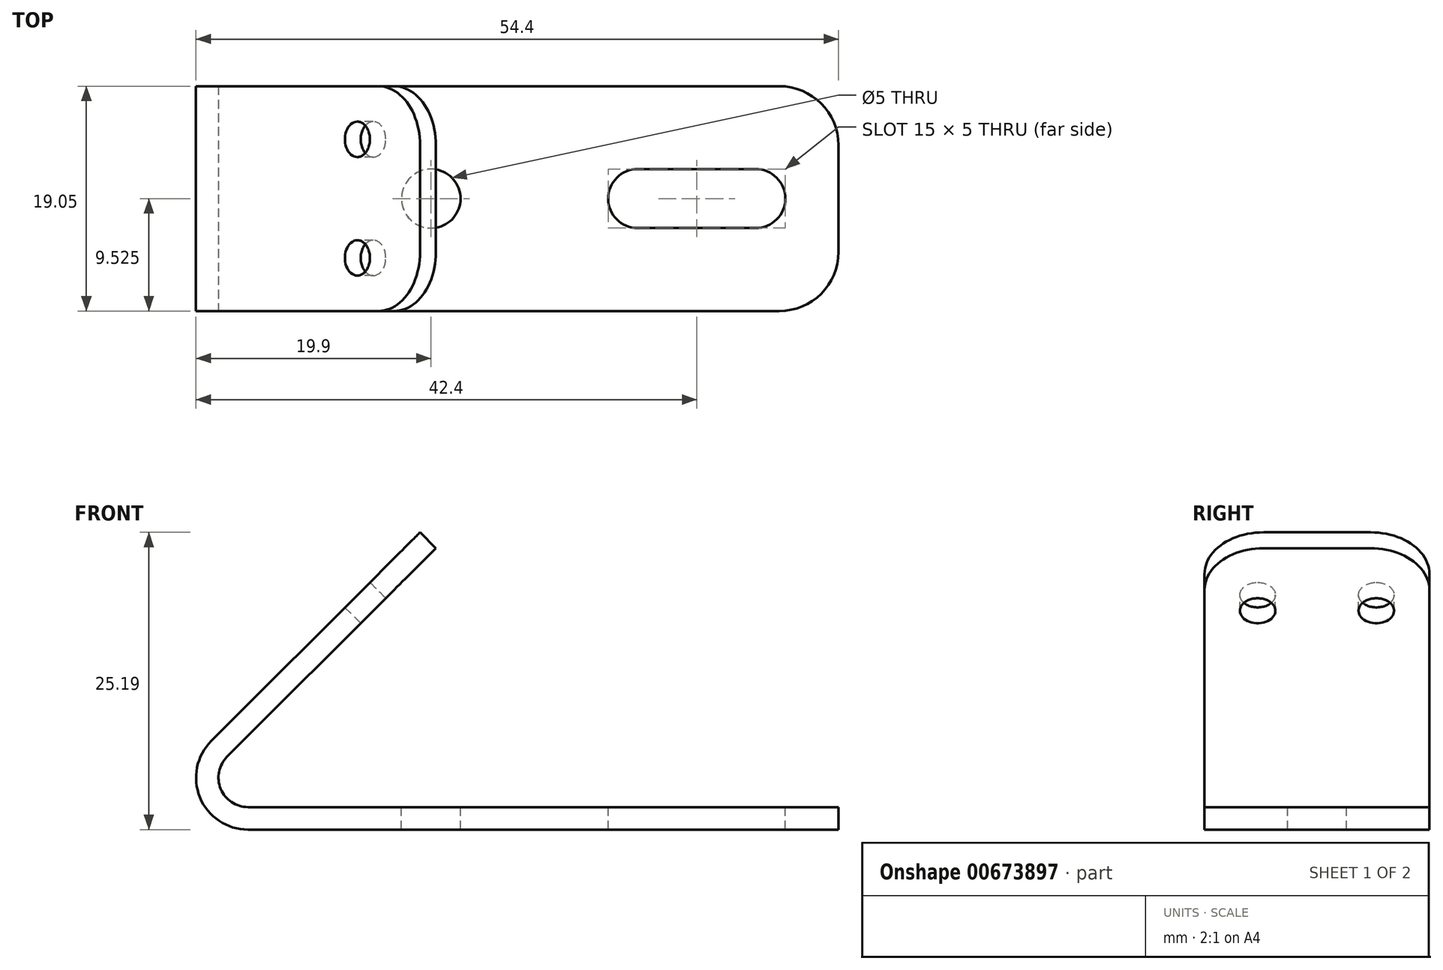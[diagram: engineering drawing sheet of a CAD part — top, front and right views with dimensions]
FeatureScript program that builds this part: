
annotation { "Feature Type Name" : "Feature", "Feature Type Description" : "" }
export const myFeature = defineFeature(function(context is Context, id is Id, definition is map)
    precondition{}
    {
        {
            var Q0;
            Q0=qCreatedBy(makeId("Front.planeOp"),FACE);
            var sketch = newSketch(context, id + "F0", { "sketchPlane" : qUnion([Q0])});
            skLineSegment(sketch, "E0", {"start": v(0, 0) * mm, "end": v(-50, 0) * mm});
            skLineSegment(sketch, "E1", {"start": v(-35.43, 25.19) * mm, "end": v(-53.11, 7.51) * mm});
            skArc(sketch, "E2", {"start": v(-53.11, 7.51) * mm, "mid": v(-54.07, 2.72) * mm, "end": v(-50, 0) * mm});
            skArc(sketch, "E3", {"start": v(-51.77, 6.17) * mm, "mid": v(-52.3, 3.44) * mm, "end": v(-50, 1.9) * mm});
            skLineSegment(sketch, "E4", {"start": v(-50, 1.9) * mm, "end": v(0, 1.9) * mm});
            skLineSegment(sketch, "E5", {"start": v(0, 1.9) * mm, "end": v(0, 0) * mm});
            skLineSegment(sketch, "E6", {"start": v(-35.43, 25.19) * mm, "end": v(-34.1, 23.85) * mm});
            skLineSegment(sketch, "E7", {"start": v(-34.1, 23.85) * mm, "end": v(-51.77, 6.17) * mm});
            skSolve(sketch);
        }
        {
            var Q0;
            Q0=makeQuery(id+"F0.imprint","IMPRINT",FACE,{"disambiguationData":[TD([[makeQuery(id+"F0.imprint","IMPRINT",EDGE,{"derivedFrom":sQuery(id+"F0.wireOp",EDGE,"E0")}),-1.0]])]});
            extrude(context, id + "F1", {"entities" : qUnion([Q0]), "oppositeDirection" : true, "depth" : 19.05 * mm, "offsetDistance" : 25 * mm});
        }
        {
            var Q0;
            Q0=makeQuery(id+"F1.opExtrude","SWEPT_FACE",FACE,{"disambiguationData":[OSD([sQuery(id+"F0.wireOp",EDGE,"E4")])]});
            var sketch = newSketch(context, id + "F2", { "sketchPlane" : qUnion([Q0])});
            skLineSegment(sketch, "E8", {"start": v(0, 9.53) * mm, "end": v(-33.34, 9.53) * mm, "construction": true});
            skLineSegment(sketch, "E9.bottom", {"start": v(-7, 7.03) * mm, "end": v(-17, 7.03) * mm});
            skLineSegment(sketch, "E9.top", {"start": v(-7, 12.03) * mm, "end": v(-17, 12.03) * mm});
            skPoint(sketch, "E9.middle", {"position": v(-12, 9.53) * mm});
            skArc(sketch, "E10", {"start": v(-7, 12.03) * mm, "mid": v(-4.5, 9.53) * mm, "end": v(-7, 7.03) * mm});
            skArc(sketch, "E11", {"start": v(-17, 7.03) * mm, "mid": v(-19.5, 9.53) * mm, "end": v(-17, 12.03) * mm});
            skPoint(sketch, "E12.orphan", {"position": v(-24, 9.53) * mm});
            skCircle(sketch, "E13", {"center": v(-34.5, 9.53) * mm, "radius": 2.5 * mm});
            skSolve(sketch);
        }
        {
            var Q0;
            Q0=makeQuery(id+"F2.imprint","IMPRINT",FACE,{"disambiguationData":[TD([[makeQuery(id+"F2.imprint","IMPRINT",EDGE,{"derivedFrom":sQuery(id+"F2.wireOp",EDGE,"E9.bottom")}),-1.0]])]});
            var Q1;
            Q1=makeQuery(id+"F2.imprint","IMPRINT",FACE,{"disambiguationData":[TD([[makeQuery(id+"F2.imprint","IMPRINT",EDGE,{"derivedFrom":sQuery(id+"F2.wireOp",EDGE,"E13")}),1.0]])]});
            extrude(context, id + "F3", {"entities" : qUnion([Q0, Q1]), "operationType" : NewBodyOperationType.REMOVE, "oppositeDirection" : true, "depth" : 25 * mm, "offsetDistance" : 25 * mm});
        }
        {
            var Q0;
            Q0=makeQuery(id+"F1.opExtrude","SWEPT_FACE",FACE,{"disambiguationData":[OSD([sQuery(id+"F0.wireOp",EDGE,"E1")])]});
            var sketch = newSketch(context, id + "F4", { "sketchPlane" : qUnion([Q0])});
            skLineSegment(sketch, "E14", {"start": v(-4.5, -32.24) * mm, "end": v(-4.5, -7.24) * mm, "construction": true});
            skLineSegment(sketch, "E15", {"start": v(-14.55, -32.24) * mm, "end": v(-14.55, -7.24) * mm, "construction": true});
            skCircle(sketch, "E16", {"center": v(-4.5, -14.74) * mm, "radius": 1.5 * mm});
            skCircle(sketch, "E17", {"center": v(-14.55, -14.74) * mm, "radius": 1.5 * mm});
            skSolve(sketch);
        }
        {
            var Q0;
            Q0=makeQuery(id+"F4.imprint","IMPRINT",FACE,{"disambiguationData":[TD([[makeQuery(id+"F4.imprint","IMPRINT",EDGE,{"derivedFrom":sQuery(id+"F4.wireOp",EDGE,"E16")}),1.0]])]});
            var Q1;
            Q1=makeQuery(id+"F4.imprint","IMPRINT",FACE,{"disambiguationData":[TD([[makeQuery(id+"F4.imprint","IMPRINT",EDGE,{"derivedFrom":sQuery(id+"F4.wireOp",EDGE,"E17")}),1.0]])]});
            extrude(context, id + "F5", {"entities" : qUnion([Q0, Q1]), "operationType" : NewBodyOperationType.REMOVE, "oppositeDirection" : true, "depth" : 7.9 * mm, "offsetDistance" : 25 * mm});
        }
        {
            var Q0;
            Q0=makeQuery(id+"F1.opExtrude","CAP_EDGE",EDGE,{"disambiguationData":[OSD([sQuery(id+"F0.wireOp",EDGE,"E5")])],"isStart":false});
            fillet(context, id + "F6", {"entities" : qUnion([Q0]), "radius" : 5 * mm, "tangentPropagation" : true, "allowEdgeOverflow" : false});
        }
        {
            var Q0;
            Q0=makeQuery(id+"F1.opExtrude","CAP_EDGE",EDGE,{"disambiguationData":[OSD([sQuery(id+"F0.wireOp",EDGE,"E5")])],"isStart":true});
            var Q1;
            Q1=makeQuery(id+"F1.opExtrude","CAP_EDGE",EDGE,{"disambiguationData":[OSD([sQuery(id+"F0.wireOp",EDGE,"E6")])],"isStart":true});
            var Q2;
            Q2=makeQuery(id+"F1.opExtrude","CAP_EDGE",EDGE,{"disambiguationData":[OSD([sQuery(id+"F0.wireOp",EDGE,"E6")])],"isStart":false});
            fillet(context, id + "F7", {"entities" : qUnion([Q0, Q1, Q2]), "radius" : 5 * mm, "tangentPropagation" : true, "allowEdgeOverflow" : false});
        }
    });
